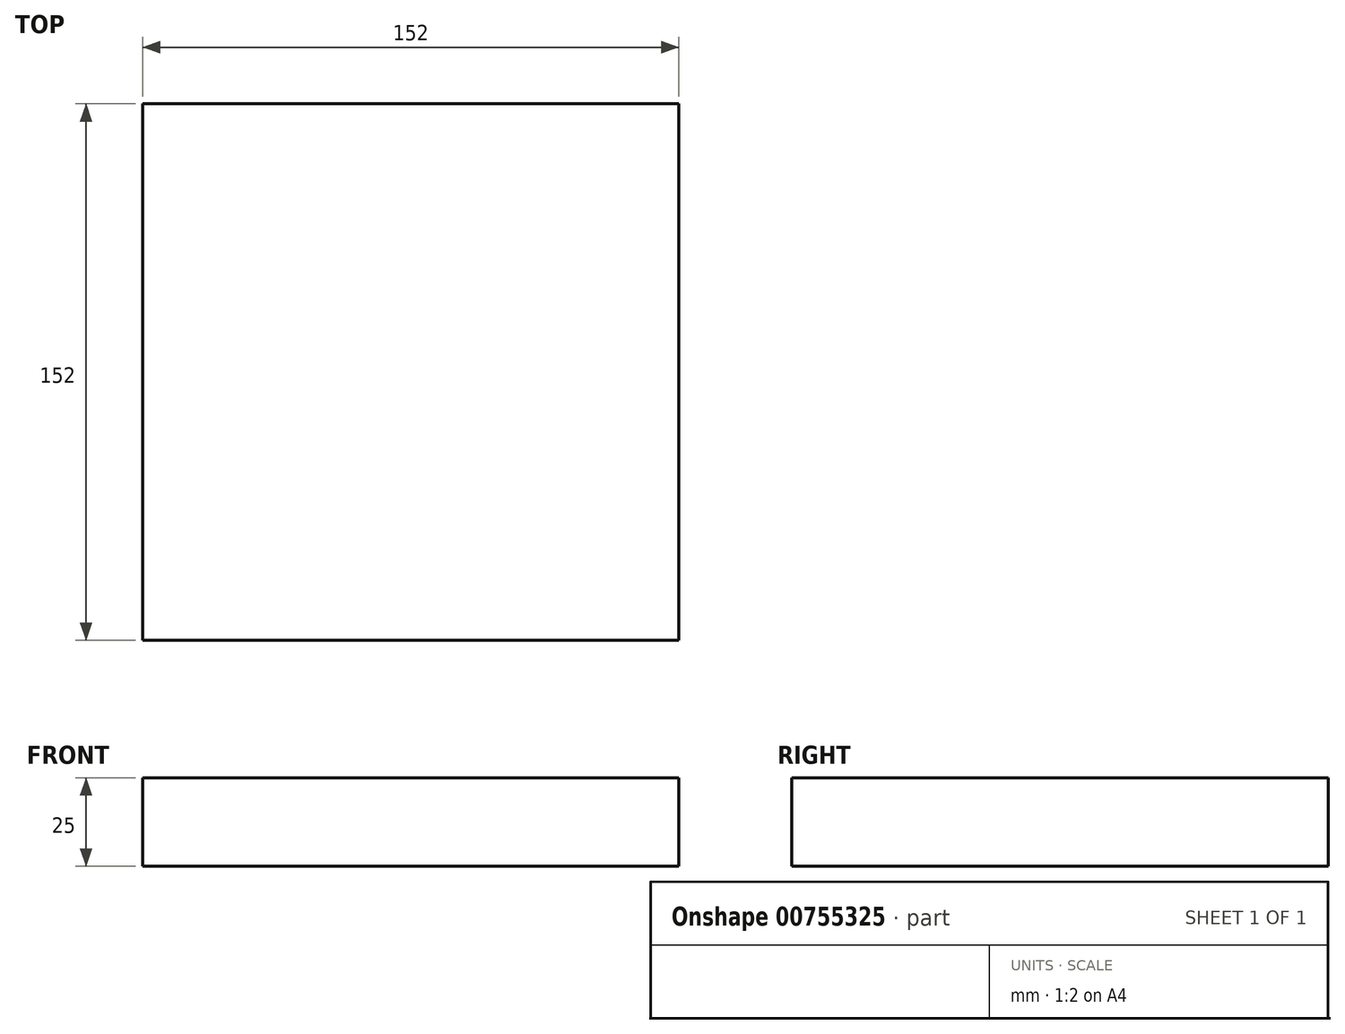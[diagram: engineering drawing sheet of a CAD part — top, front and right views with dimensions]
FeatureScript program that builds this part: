
annotation { "Feature Type Name" : "Feature", "Feature Type Description" : "" }
export const myFeature = defineFeature(function(context is Context, id is Id, definition is map)
    precondition{}
    {
        {
            var Q0;
            Q0=qCreatedBy(makeId("Top.planeOp"),FACE);
            var sketch = newSketch(context, id + "F0", { "sketchPlane" : qUnion([Q0])});
            skLineSegment(sketch, "E0.bottom", {"start": v(76, 76) * mm, "end": v(-76, 76) * mm});
            skLineSegment(sketch, "E0.top", {"start": v(76, -76) * mm, "end": v(-76, -76) * mm});
            skLineSegment(sketch, "E0.left", {"start": v(76, 76) * mm, "end": v(76, -76) * mm});
            skLineSegment(sketch, "E0.right", {"start": v(-76, 76) * mm, "end": v(-76, -76) * mm});
            skPoint(sketch, "E0.middle", {"position": v(0, 0) * mm});
            skSolve(sketch);
        }
        {
            var Q0;
            Q0=makeQuery(id+"F0.imprint","IMPRINT",FACE,{"disambiguationData":[TD([[makeQuery(id+"F0.imprint","IMPRINT",EDGE,{"derivedFrom":sQuery(id+"F0.wireOp",EDGE,"E0.bottom")}),1.0]])]});
            extrude(context, id + "F1", {"entities" : qUnion([Q0]), "depth" : 25 * mm, "offsetDistance" : 25 * mm});
        }
    });
